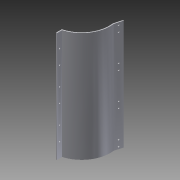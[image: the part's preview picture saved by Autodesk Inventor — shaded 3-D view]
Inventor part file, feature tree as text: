
AUTODESK INVENTOR PART (.ipt)
format: ipt  version: 2015 (Build 190159000, 159)  size: 139,776 bytes
history: native  units: mm
features: extrude x3, sketch x3, pattern_linear x2
ambient origin geometry x8: Origin, YZ Plane, XZ Plane, XY Plane, X Axis, Y Axis, Z Axis, Center Point
bodies: 实体1 (feature_tree)
feature tree (8):
  extrude  "拉伸1"  Depth=50.0mm
  extrude  "拉伸2"  Depth=3.0mm
  pattern_linear  "矩形阵列1"  Spacing1=3.0mm  [1 undecoded]
  extrude  "拉伸3"  Depth=3.0mm
  pattern_linear  "矩形阵列2"  Spacing1=25.0mm  [1 undecoded]
  sketch  "草图1"  dims[d0=200.0mm d1=50.0mm]
  sketch  "草图2"  dims[d2=18.0mm d3=3.0mm]
  sketch  "草图3"  dims[d4=3.0mm d5=3.0mm d6=200.0mm d7=25.0mm d8=25.0mm d9=5.0mm d10=300.0mm d11=30.0mm d12=398.0mm d13=0.0mm d14=5.0mm d15=5.0mm d16=10.0mm d17=10.0mm d18=53.0mm d19=105.0mm d20=3.0mm d21=0.0mm d22=30.0mm d24=120.0mm d25=5.0mm d26=5.0mm d27=15.0mm d28=15.0mm d29=8.0mm d30=30.0mm d31=3.0mm d32=0.0mm d33=40.0mm d35=120.0mm]
note: 2 required parameter values undecoded (feature->parameter linkage not recoverable at this tier; creation-order binding heuristic only, values carry confidence <= 0.55)
